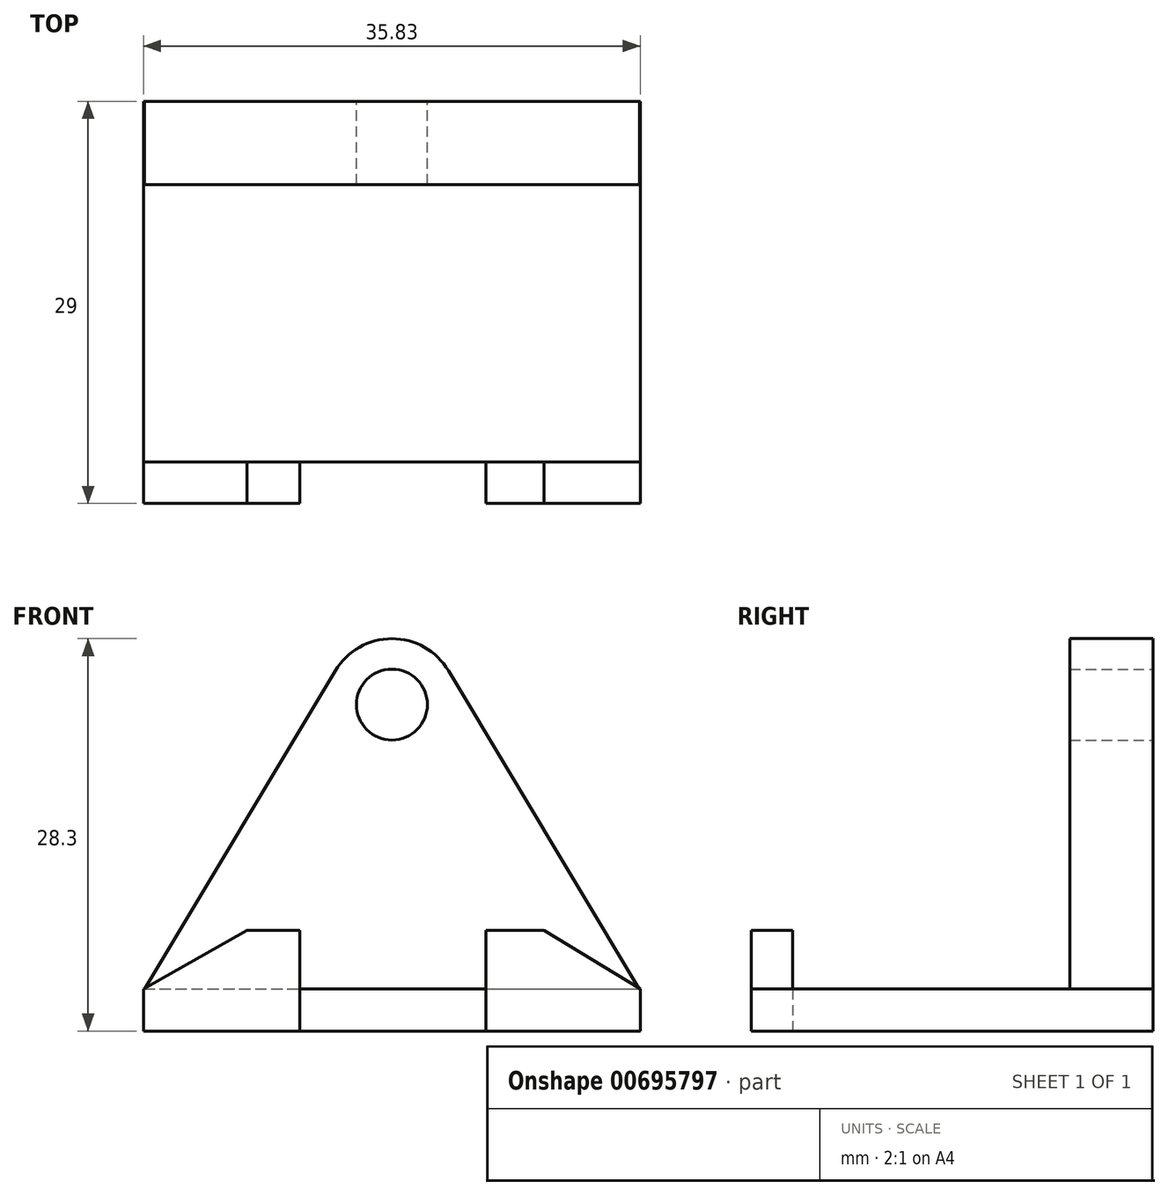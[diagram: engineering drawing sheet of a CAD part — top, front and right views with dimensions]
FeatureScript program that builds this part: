
annotation { "Feature Type Name" : "Feature", "Feature Type Description" : "" }
export const myFeature = defineFeature(function(context is Context, id is Id, definition is map)
    precondition{}
    {
        {
            var Q0;
            Q0=qCreatedBy(makeId("Front.planeOp"),FACE);
            var sketch = newSketch(context, id + "F0", { "sketchPlane" : qUnion([Q0])});
            skLineSegment(sketch, "E0", {"start": v(0, 0) * mm, "end": v(35.83, 0) * mm});
            skLineSegment(sketch, "E1", {"start": v(35.83, 0) * mm, "end": v(35.83, 3.02) * mm});
            skLineSegment(sketch, "E2", {"start": v(0, 3.02) * mm, "end": v(0, 0) * mm});
            skLineSegment(sketch, "E3", {"start": v(0, 3.02) * mm, "end": v(35.83, 3.02) * mm});
            skSolve(sketch);
        }
        {
            var Q0;
            Q0 = qSketchRegion(id + "F0", true);
            extrude(context, id + "F1", {"entities" : qUnion([Q0]), "depth" : 26 * mm, "offsetDistance" : 25 * mm});
        }
        {
            var Q0;
            Q0=qCreatedBy(makeId("Front.planeOp"),FACE);
            var sketch = newSketch(context, id + "F2", { "sketchPlane" : qUnion([Q0])});
            skLineSegment(sketch, "E4", {"start": v(35.83, 2.91) * mm, "end": v(0, 2.91) * mm});
            skArc(sketch, "E5", {"start": v(22, 25.99) * mm, "mid": v(17.92, 28.3) * mm, "end": v(13.84, 25.99) * mm});
            skLineSegment(sketch, "E6", {"start": v(35.83, 2.91) * mm, "end": v(22, 25.99) * mm});
            skLineSegment(sketch, "E7", {"start": v(0, 2.91) * mm, "end": v(13.84, 25.99) * mm});
            skCircle(sketch, "E8", {"center": v(17.92, 23.54) * mm, "radius": 2.56 * mm});
            skSolve(sketch);
        }
        {
            var Q0;
            Q0 = qSketchRegion(id + "F2", true);
            extrude(context, id + "F3", {"entities" : qUnion([Q0]), "operationType" : NewBodyOperationType.ADD, "depth" : 6 * mm, "offsetDistance" : 25 * mm});
        }
        {
            var Q0;
            Q0=makeQuery(id+"F1.opExtrude","CAP_FACE",FACE,{"disambiguationData":[OSD([sQuery(id+"F0.wireOp",EDGE,"E0"),sQuery(id+"F0.wireOp",EDGE,"E1"),sQuery(id+"F0.wireOp",EDGE,"E2"),sQuery(id+"F0.wireOp",EDGE,"E3")])],"isStart":false});
            var sketch = newSketch(context, id + "F4", { "sketchPlane" : qUnion([Q0])});
            skLineSegment(sketch, "E9", {"start": v(0, 0) * mm, "end": v(0, 3.02) * mm});
            skLineSegment(sketch, "E10", {"start": v(0, 3.02) * mm, "end": v(7.46, 7.27) * mm});
            skLineSegment(sketch, "E11", {"start": v(7.46, 7.27) * mm, "end": v(11.27, 7.27) * mm});
            skLineSegment(sketch, "E12", {"start": v(11.27, 7.27) * mm, "end": v(11.27, 0) * mm});
            skLineSegment(sketch, "E13", {"start": v(11.27, 0) * mm, "end": v(0, 0) * mm});
            skLineSegment(sketch, "E14", {"start": v(35.83, 0) * mm, "end": v(35.83, 3.02) * mm});
            skLineSegment(sketch, "E15", {"start": v(35.83, 3.02) * mm, "end": v(28.9, 7.27) * mm});
            skLineSegment(sketch, "E16", {"start": v(28.9, 7.27) * mm, "end": v(24.69, 7.27) * mm});
            skLineSegment(sketch, "E17", {"start": v(24.69, 7.27) * mm, "end": v(24.69, 0) * mm});
            skLineSegment(sketch, "E18", {"start": v(24.69, 0) * mm, "end": v(35.83, 0) * mm});
            skSolve(sketch);
        }
        {
            var Q0;
            Q0 = qSketchRegion(id + "F4", true);
            extrude(context, id + "F5", {"entities" : qUnion([Q0]), "operationType" : NewBodyOperationType.ADD, "depth" : 3 * mm, "offsetDistance" : 25 * mm});
        }
    });
